# Revit family: xled_pro_wide_sl_010232
name_source: partatom
category: Leuchten
revit_build: Autodesk Revit 2016 (Build: 20190508_0715(x64)
units: mm (PartAtom-declared; Revit-internal decimal feet)

## family parameters
Basisbauteil = Fläche
Beim Laden mit Abzugskörper schneiden = Nein
Bemaßung runder Anschluss = Durchmesser verwenden
Gemeinsam genutzt = Nein
Lichtquelle = Nein
Raumberechnungspunkt = Nein
Teiletyp = Normal

## types (1)
- XLED PRO Wide SL (1 x , 2400 lm, 4000 K)
    Beschreibung = Dimensions (L x W x H): 126 x 265 x 165 mm; Mains power supply: 220 – 240 V / 50 – 60 Hz; Output: 24,8 W; Luminous flux: 2400 lm; Colour temperature: 4000 K; Colour variation LED: SDCM3; Colour Rendering Index CRI: 80-89; With lamp: Yes, STEINEL LED system; Lamp: LED cannot be replaced; LED life expectancy (max. °C): 50000 h; Drop in luminous flux in accordance with LM80: L70B10; LED cooling system: Passive Thermo Control; With motion detector: No; Photo-cell controller: No; Basic light level function: No; Soft light start: No; Continuous light: selectable, 4h; Impact resistance: IK03; IP-rating: IP54; Protection class: I; Ambient temperature: -20 – 40 °C; Housing material: Aluminium; Cover material: Plastic, transparent; Manufacturer's Warranty: 5 years; PU1, net weight: 1,827 kg; Version: white; PU1, EAN: 4007841010232
    CIE Flux Codes = 47 82 96 99 102
    Color Rendering = 80-89
    Color Temperature = 4000 K
    Frequency = 60 Hz, 50 Hz
    Height = 165 mm
    Hersteller = Steinel
    Lamp Light Flux = 2400 lm
    Lamp count = 1
    Lampe = 1 x
    Length = 126 mm
    Luminous efficacy = 100 lm/W
    ModVariant = Nein
    Modell = 010232
    Mounting Type = Surface mounted
    Number of Poles = 1
    OnlyDefault = Ja
    Power Factor = 1
    Product Name = XLED PRO Wide SL
    Product group = Sensor-switched indoor light
    ProductGroupID = 30
    Protection Class = Protection class I
    Protection Degree = IP 54
    RlxData = <blob elided: 50405 chars, md5=f8ef7b0d>
    Scheinlast = 24 VA
    Socket = socket
    Standby Power = 0 W
    System Light Flux = 2400 lm
    System Power = 24 W
    Typenbild = produkt1_010232.jpg
    Typenkommentare = Product without accessories
    URL = http://relux.com
    VarID = ---
    Voltage = 0 V
    Vorgabe-Ansicht = 1800 mm
    Weight = 0.00 kg
    Width = 265 mm

## geometry (parser evidence)
native form markers: Blend x4, Sweep x14
no freeform markers — native parametric forms only
